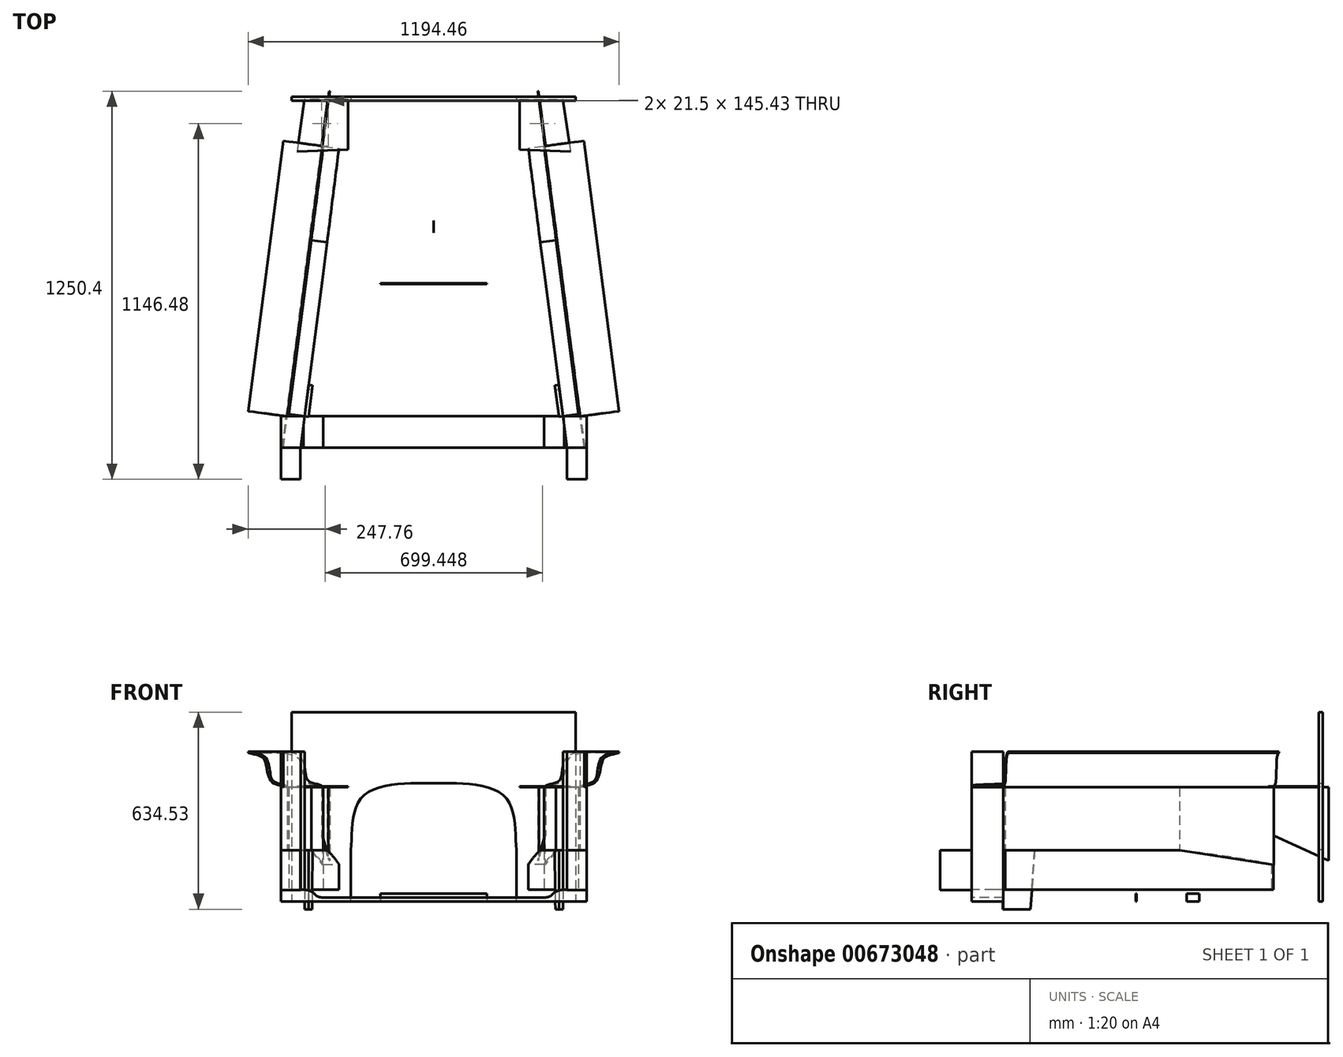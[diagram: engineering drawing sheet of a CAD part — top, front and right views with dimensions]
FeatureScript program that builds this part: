
annotation { "Feature Type Name" : "Feature", "Feature Type Description" : "" }
export const myFeature = defineFeature(function(context is Context, id is Id, definition is map)
    precondition{}
    {
        {
            var Q0;
            Q0=qCreatedBy(makeId("Top.planeOp"),FACE);
            var sketch = newSketch(context, id + "F0", { "sketchPlane" : qUnion([Q0])});
            skLineSegment(sketch, "E0.bottom", {"start": v(0, 0) * mm, "end": v(711.2, 0) * mm});
            skLineSegment(sketch, "E0.top", {"start": v(0, -101.6) * mm, "end": v(711.2, -101.6) * mm});
            skLineSegment(sketch, "E0.left", {"start": v(0, 0) * mm, "end": v(0, -101.6) * mm});
            skLineSegment(sketch, "E0.right", {"start": v(711.2, 0) * mm, "end": v(711.2, -101.6) * mm});
            skLineSegment(sketch, "E1", {"start": v(711.2, -101.6) * mm, "end": v(784.23, -101.6) * mm});
            skLineSegment(sketch, "E2", {"start": v(0, -101.6) * mm, "end": v(-73.03, -101.6) * mm});
            skLineSegment(sketch, "E3", {"start": v(711.2, 0) * mm, "end": v(771.52, 0) * mm});
            skLineSegment(sketch, "E4", {"start": v(0, 0) * mm, "end": v(-60.33, 0) * mm});
            skLineSegment(sketch, "E5", {"start": v(-60.33, 0) * mm, "end": v(-73.03, -101.6) * mm});
            skLineSegment(sketch, "E6", {"start": v(771.52, 0) * mm, "end": v(784.23, -101.6) * mm});
            skLineSegment(sketch, "E7", {"start": v(784.23, -101.6) * mm, "end": v(847.73, -101.6) * mm});
            skLineSegment(sketch, "E8", {"start": v(847.73, -101.6) * mm, "end": v(847.73, 0) * mm});
            skLineSegment(sketch, "E9", {"start": v(847.73, 0) * mm, "end": v(771.52, 0) * mm});
            skLineSegment(sketch, "E10", {"start": v(-73.03, -101.6) * mm, "end": v(-136.53, -101.6) * mm});
            skLineSegment(sketch, "E11", {"start": v(-136.53, -101.6) * mm, "end": v(-136.53, 0) * mm});
            skLineSegment(sketch, "E12", {"start": v(-136.53, 0) * mm, "end": v(-60.33, 0) * mm});
            skLineSegment(sketch, "E13", {"start": v(355.6, 0) * mm, "end": v(355.6, 428.63) * mm});
            skLineSegment(sketch, "E14", {"start": v(355.6, 428.63) * mm, "end": v(527.05, 428.63) * mm});
            skLineSegment(sketch, "E15", {"start": v(355.6, 428.63) * mm, "end": v(184.15, 428.63) * mm});
            skLineSegment(sketch, "E16", {"start": v(184.15, 428.63) * mm, "end": v(184.15, 426.09) * mm});
            skLineSegment(sketch, "E17", {"start": v(184.15, 426.09) * mm, "end": v(527.05, 426.09) * mm});
            skLineSegment(sketch, "E18", {"start": v(527.05, 426.09) * mm, "end": v(527.05, 428.63) * mm});
            skLineSegment(sketch, "E19", {"start": v(355.6, 428.63) * mm, "end": v(355.6, 438.15) * mm});
            skLineSegment(sketch, "E20", {"start": v(355.6, 438.15) * mm, "end": v(-3.17, 438.15) * mm});
            skLineSegment(sketch, "E21", {"start": v(355.6, 438.15) * mm, "end": v(714.35, 438.15) * mm});
            skLineSegment(sketch, "E22", {"start": v(-60.32, 0) * mm, "end": v(-3.17, 438.15) * mm});
            skLineSegment(sketch, "E23", {"start": v(714.35, 438.15) * mm, "end": v(771.52, 0) * mm});
            skLineSegment(sketch, "E24", {"start": v(-3.18, 438.15) * mm, "end": v(50.79, 862.83) * mm});
            skLineSegment(sketch, "E25", {"start": v(50.79, 862.83) * mm, "end": v(660.39, 862.83) * mm});
            skLineSegment(sketch, "E26", {"start": v(660.39, 862.83) * mm, "end": v(714.35, 438.15) * mm});
            skLineSegment(sketch, "E27", {"start": v(660.39, 862.83) * mm, "end": v(710.78, 869.23) * mm});
            skLineSegment(sketch, "E28", {"start": v(771.52, 0) * mm, "end": v(821.9, 6.57) * mm});
            skLineSegment(sketch, "E29", {"start": v(710.78, 869.23) * mm, "end": v(821.9, 6.57) * mm});
            skLineSegment(sketch, "E30", {"start": v(660.39, 862.83) * mm, "end": v(622.29, 862.83) * mm});
            skLineSegment(sketch, "E31", {"start": v(50.79, 862.83) * mm, "end": v(88.89, 862.83) * mm});
            skLineSegment(sketch, "E32", {"start": v(355.6, 0) * mm, "end": v(355.6, 1016) * mm});
            skLineSegment(sketch, "E33", {"start": v(355.6, 1016) * mm, "end": v(812.8, 1016) * mm});
            skLineSegment(sketch, "E34.MirrorCS", {"start": v(50.81, 862.83) * mm, "end": v(0.42, 869.23) * mm});
            skLineSegment(sketch, "E35.MirrorCS", {"start": v(0.42, 869.23) * mm, "end": v(-110.7, 6.57) * mm});
            skLineSegment(sketch, "E36.MirrorCS", {"start": v(-60.32, 0) * mm, "end": v(-110.7, 6.57) * mm});
            skLineSegment(sketch, "E37.MirrorCS", {"start": v(-136.53, 0) * mm, "end": v(-60.32, 0) * mm});
            skLineSegment(sketch, "E38.MirrorCS", {"start": v(-136.52, -101.6) * mm, "end": v(-136.52, 0) * mm});
            skLineSegment(sketch, "E39", {"start": v(355.6, 630.77) * mm, "end": v(355.85, 630.77) * mm});
            skLineSegment(sketch, "E40", {"start": v(355.85, 630.77) * mm, "end": v(355.85, 590.81) * mm});
            skLineSegment(sketch, "E41", {"start": v(355.85, 590.81) * mm, "end": v(355.6, 590.81) * mm});
            skLineSegment(sketch, "E42", {"start": v(355.6, 1016) * mm, "end": v(-101.6, 1016) * mm});
            skLineSegment(sketch, "E43", {"start": v(-101.6, 1016) * mm, "end": v(-101.6, 1028.7) * mm});
            skLineSegment(sketch, "E44", {"start": v(-101.6, 1028.7) * mm, "end": v(813.04, 1028.7) * mm});
            skLineSegment(sketch, "E45", {"start": v(813.04, 1028.7) * mm, "end": v(812.8, 1016) * mm});
            skSolve(sketch);
        }
        {
            var Q0;
            Q0=makeQuery(id+"F0.imprint","IMPRINT",FACE,{"disambiguationData":[TD([[makeQuery(id+"F0.imprint","IMPRINT",EDGE,{"derivedFrom":sQuery(id+"F0.wireOp",EDGE,"E0.top")}),1.0]])]});
            extrude(context, id + "F1", {"entities" : qUnion([Q0]), "depth" : 12.7 * mm, "offsetDistance" : 25.4 * mm});
        }
        {
            var Q0;
            Q0=makeQuery(id+"F0.imprint","IMPRINT",FACE,{"disambiguationData":[TD([[makeQuery(id+"F0.imprint","IMPRINT",EDGE,{"derivedFrom":sQuery(id+"F0.wireOp",EDGE,"E0.right")}),1.0]])]});
            extrude(context, id + "F2", {"entities" : qUnion([Q0]), "operationType" : NewBodyOperationType.ADD, "depth" : 38.1 * mm, "offsetDistance" : 25.4 * mm});
        }
        {
            var Q0;
            Q0=makeQuery(id+"F0.imprint","IMPRINT",FACE,{"disambiguationData":[TD([[makeQuery(id+"F0.imprint","IMPRINT",EDGE,{"derivedFrom":sQuery(id+"F0.wireOp",EDGE,"E6")}),1.0]])]});
            extrude(context, id + "F3", {"entities" : qUnion([Q0]), "operationType" : NewBodyOperationType.ADD, "depth" : 482.6 * mm, "offsetDistance" : 25.4 * mm});
        }
        {
            var Q0;
            Q0=makeQuery(id+"F0.imprint","IMPRINT",FACE,{"disambiguationData":[TD([[makeQuery(id+"F0.imprint","IMPRINT",EDGE,{"derivedFrom":sQuery(id+"F0.wireOp",EDGE,"E23")}),1.0]])]});
            extrude(context, id + "F4", {"entities" : qUnion([Q0]), "depth" : 165.1 * mm, "offsetDistance" : 25.4 * mm});
        }
        {
            var Q0;
            Q0=makeQuery(id+"F0.imprint","IMPRINT",FACE,{"disambiguationData":[TD([[makeQuery(id+"F0.imprint","IMPRINT",EDGE,{"derivedFrom":sQuery(id+"F0.wireOp",EDGE,"E23")}),1.0]])]});
            extrude(context, id + "F5", {"entities" : qUnion([Q0]), "operationType" : NewBodyOperationType.REMOVE, "depth" : 38.1 * mm, "offsetDistance" : 25.4 * mm});
        }
        {
            var Q0;
            Q0=makeQuery(id+"F4.opExtrude","SWEPT_FACE",FACE,{"disambiguationData":[OSD([sQuery(id+"F0.wireOp",EDGE,"E26")])]});
            var sketch = newSketch(context, id + "F6", { "sketchPlane" : qUnion([Q0])});
            skPoint(sketch, "E46.1.internal.snap0", {"position": v(-467.9, 143.2) * mm});
            skFitSpline(sketch, "E46", {"points": [v(-467.9, 165.1) * mm, v(-633.83, 143.2) * mm, v(-772.7, 119.15) * mm], "startDerivative": vector(-344.98, -40.08) * mm, "endDerivative": vector(-262.21, -52.17) * mm});
            skLineSegment(sketch, "E47", {"start": v(-772.7, 119.15) * mm, "end": v(-772.7, 165.1) * mm});
            skLineSegment(sketch, "E48", {"start": v(-772.7, 165.1) * mm, "end": v(-467.9, 165.1) * mm});
            skSolve(sketch);
        }
        {
            var Q0;
            Q0=makeQuery(id+"F6.imprint","IMPRINT",FACE,{"disambiguationData":[TD([[makeQuery(id+"F6.imprint","IMPRINT",EDGE,{"derivedFrom":sQuery(id+"F6.wireOp",EDGE,"E46")}),-1.0]])]});
            extrude(context, id + "F7", {"entities" : qUnion([Q0]), "operationType" : NewBodyOperationType.REMOVE, "oppositeDirection" : true, "depth" : 53.34 * mm, "offsetDistance" : 25.4 * mm});
        }
        {
            var Q0;
            Q0=makeQuery(id+"F4.opExtrude","CAP_FACE",FACE,{"disambiguationData":[OSD([sQuery(id+"F0.wireOp",EDGE,"E23"),sQuery(id+"F0.wireOp",EDGE,"E26"),sQuery(id+"F0.wireOp",EDGE,"E27"),sQuery(id+"F0.wireOp",EDGE,"E28"),sQuery(id+"F0.wireOp",EDGE,"E29")])],"isStart":false});
            var sketch = newSketch(context, id + "F8", { "sketchPlane" : qUnion([Q0])});
            skLineSegment(sketch, "E49", {"start": v(749.72, 566.93) * mm, "end": v(752.87, 567.33) * mm});
            skLineSegment(sketch, "E50", {"start": v(752.87, 567.33) * mm, "end": v(826.9, 0) * mm});
            skLineSegment(sketch, "E51", {"start": v(826.9, 0) * mm, "end": v(771.52, 0) * mm});
            skLineSegment(sketch, "E52", {"start": v(771.52, 0) * mm, "end": v(821.9, 6.57) * mm});
            skLineSegment(sketch, "E53", {"start": v(821.9, 6.57) * mm, "end": v(749.72, 566.93) * mm});
            skSolve(sketch);
        }
        {
            var Q0;
            Q0=makeQuery(id+"F8.imprint","IMPRINT",FACE,{"disambiguationData":[TD([[makeQuery(id+"F8.imprint","IMPRINT",EDGE,{"derivedFrom":sQuery(id+"F8.wireOp",EDGE,"E49")}),-1.0]])]});
            extrude(context, id + "F9", {"entities" : qUnion([Q0]), "operationType" : NewBodyOperationType.ADD, "depth" : 203.2 * mm, "offsetDistance" : 25.4 * mm});
        }
        {
            var Q0;
            Q0=makeQuery(id+"F3.boolean.opBoolean","MERGE",FACE,{"derivedFrom":[makeQuery(id+"F2.boolean.opBoolean","MERGE",FACE,{"derivedFrom":[makeQuery(id+"F1.opExtrude","SWEPT_FACE",FACE,{"disambiguationData":[OSD([sQuery(id+"F0.wireOp",EDGE,"E0.top")])]}),makeQuery(id+"F2.opExtrude","SWEPT_FACE",FACE,{"disambiguationData":[OSD([sQuery(id+"F0.wireOp",EDGE,"E1")])]})]}),makeQuery(id+"F3.opExtrude","SWEPT_FACE",FACE,{"disambiguationData":[OSD([sQuery(id+"F0.wireOp",EDGE,"E7")])]})]});
            var sketch = newSketch(context, id + "F10", { "sketchPlane" : qUnion([Q0])});
            skLineSegment(sketch, "E54", {"start": v(711.2, 12.7) * mm, "end": v(711.2, 38.1) * mm});
            skLineSegment(sketch, "E55", {"start": v(711.2, 38.1) * mm, "end": v(784.23, 38.1) * mm});
            skFitSpline(sketch, "E56", {"points": [v(784.23, 38.1) * mm, v(745.92, 30.04) * mm, v(734.41, 19.42) * mm, v(711.2, 12.7) * mm], "startDerivative": vector(-114.1, 5.7) * mm, "endDerivative": vector(-138.93, -12.85) * mm});
            skSolve(sketch);
        }
        {
            var Q0;
            {var subQ0=sQuery(id+"F10.wireOp",EDGE,"E54");Q0=makeQuery(id+"F10.imprint","IMPRINT",FACE,{"disambiguationData":[TD([[makeQuery(id+"F10.imprint","IMPRINT",EDGE,{"derivedFrom":subQ0}),1.0]])]});}
            extrude(context, id + "F11", {"entities" : qUnion([Q0]), "operationType" : NewBodyOperationType.REMOVE, "oppositeDirection" : true, "depth" : 101.6 * mm, "offsetDistance" : 25.4 * mm});
        }
        {
            var Q0;
            {var subQ0=sQuery(id+"F0.wireOp",EDGE,"E15");Q0=makeQuery(id+"F0.imprint","IMPRINT",FACE,{"disambiguationData":[TD([[makeQuery(id+"F0.imprint","IMPRINT",EDGE,{"derivedFrom":subQ0}),1.0]])]});}
            var Q1;
            {var subQ0=sQuery(id+"F0.wireOp",EDGE,"E14");Q1=makeQuery(id+"F0.imprint","IMPRINT",FACE,{"disambiguationData":[TD([[makeQuery(id+"F0.imprint","IMPRINT",EDGE,{"derivedFrom":subQ0}),-1.0]])]});}
            extrude(context, id + "F12", {"entities" : qUnion([Q0, Q1]), "depth" : 25.4 * mm, "offsetDistance" : 25.4 * mm});
        }
        {
            var Q0;
            {var subQ0=sQuery(id+"F0.wireOp",EDGE,"E39");Q0=makeQuery(id+"F0.imprint","IMPRINT",FACE,{"disambiguationData":[TD([[makeQuery(id+"F0.imprint","IMPRINT",EDGE,{"derivedFrom":subQ0}),-1.0]])]});}
            extrude(context, id + "F13", {"entities" : qUnion([Q0]), "depth" : 25.4 * mm, "offsetDistance" : 25.4 * mm});
        }
        {
            var Q0;
            Q0=makeQuery(id+"F4.opExtrude","SWEPT_BODY",BODY,{"disambiguationData":[OSD([sQuery(id+"F0.wireOp",EDGE,"E23"),sQuery(id+"F0.wireOp",EDGE,"E26"),sQuery(id+"F0.wireOp",EDGE,"E27"),sQuery(id+"F0.wireOp",EDGE,"E28"),sQuery(id+"F0.wireOp",EDGE,"E29")])]});
            var Q1;
            Q1=makeQuery(id+"F1.opExtrude","SWEPT_BODY",BODY,{"disambiguationData":[OSD([sQuery(id+"F0.wireOp",EDGE,"E0.bottom"),sQuery(id+"F0.wireOp",EDGE,"E0.top"),sQuery(id+"F0.wireOp",EDGE,"E0.left"),sQuery(id+"F0.wireOp",EDGE,"E0.right")])]});
            var Q2;
            Q2=makeQuery(id+"F13.opExtrude","SWEPT_FACE",FACE,{"disambiguationData":[OSD([sQuery(id+"F0.wireOp",EDGE,"E32")])]});
            mirror(context, id + "F14", {"operationType" : NewBodyOperationType.ADD, "entities" : qUnion([Q0, Q1]), "mirrorPlane" : qUnion([Q2])});
        }
        {
            var Q0;
            Q0=makeQuery(id+"F9.opExtrude","SWEPT_FACE",FACE,{"disambiguationData":[OSD([sQuery(id+"F8.wireOp",EDGE,"E50")])]});
            var sketch = newSketch(context, id + "F15", { "sketchPlane" : qUnion([Q0])});
            skLineSegment(sketch, "E57", {"start": v(465.15, 368.3) * mm, "end": v(770.95, 368.3) * mm});
            skLineSegment(sketch, "E58", {"start": v(770.95, 368.3) * mm, "end": v(770.95, 118.46) * mm});
            skLineSegment(sketch, "E59", {"start": v(-107, 482.07) * mm, "end": v(770.95, 482.07) * mm});
            skLineSegment(sketch, "E60", {"start": v(770.95, 482.07) * mm, "end": v(770.95, 368.3) * mm});
            skLineSegment(sketch, "E61", {"start": v(465.15, 368.3) * mm, "end": v(465.15, 165.1) * mm});
            skLineSegment(sketch, "E62", {"start": v(465.15, 165.1) * mm, "end": v(770.95, 118.46) * mm});
            skLineSegment(sketch, "E63", {"start": v(-107, 482.07) * mm, "end": v(-107, 368.3) * mm});
            skLineSegment(sketch, "E64", {"start": v(-107, 368.3) * mm, "end": v(465.15, 368.3) * mm});
            skLineSegment(sketch, "E65", {"start": v(770.95, 368.3) * mm, "end": v(948.75, 368.3) * mm});
            skLineSegment(sketch, "E66", {"start": v(948.75, 368.3) * mm, "end": v(948.75, 131.53) * mm});
            skLineSegment(sketch, "E67", {"start": v(948.75, 131.53) * mm, "end": v(770.95, 211.96) * mm});
            skSolve(sketch);
        }
        {
            var Q0;
            Q0=makeQuery(id+"F15.imprint","IMPRINT",FACE,{"disambiguationData":[TD([[makeQuery(id+"F15.imprint","IMPRINT",EDGE,{"derivedFrom":sQuery(id+"F15.wireOp",EDGE,"E57")}),-1.0]])]});
            extrude(context, id + "F16", {"entities" : qUnion([Q0]), "oppositeDirection" : true, "depth" : 2.54 * mm, "offsetDistance" : 25.4 * mm});
        }
        {
            var Q0;
            Q0=makeQuery(id+"F15.imprint","IMPRINT",FACE,{"disambiguationData":[TD([[makeQuery(id+"F15.imprint","IMPRINT",EDGE,{"derivedFrom":sQuery(id+"F15.wireOp",EDGE,"E57")}),1.0]])]});
            extrude(context, id + "F17", {"entities" : qUnion([Q0]), "depth" : 127 * mm, "offsetDistance" : 25.4 * mm});
        }
        {
            var Q0;
            Q0=makeQuery(id+"F17.opExtrude","SWEPT_FACE",FACE,{"disambiguationData":[OSD([sQuery(id+"F15.wireOp",EDGE,"E60")])]});
            var sketch = newSketch(context, id + "F18", { "sketchPlane" : qUnion([Q0])});
            skFitSpline(sketch, "E68", {"points": [v(-819.95, 368.3) * mm, v(-869.16, 392.24) * mm, v(-946.95, 482.07) * mm], "startDerivative": vector(-53.79, 96.96) * mm, "endDerivative": vector(-444.07, 0) * mm});
            skLineSegment(sketch, "E69", {"start": v(-946.95, 482.07) * mm, "end": v(-946.95, 478.9) * mm});
            skLineSegment(sketch, "E70", {"start": v(-819.95, 368.3) * mm, "end": v(-823.13, 368.3) * mm});
            skFitSpline(sketch, "E71", {"points": [v(-946.95, 478.9) * mm, v(-892.3, 451.57) * mm, v(-864.36, 380.9) * mm, v(-823.13, 368.3) * mm], "startDerivative": vector(317.97, -76.6) * mm, "endDerivative": vector(-33.51, -59.88) * mm});
            skLineSegment(sketch, "E72", {"start": v(-946.95, 482.07) * mm, "end": v(-819.95, 482.07) * mm});
            skLineSegment(sketch, "E73", {"start": v(-819.95, 482.07) * mm, "end": v(-819.95, 368.3) * mm});
            skLineSegment(sketch, "E74", {"start": v(-823.13, 368.3) * mm, "end": v(-946.95, 368.3) * mm});
            skLineSegment(sketch, "E75", {"start": v(-946.95, 368.3) * mm, "end": v(-946.95, 478.9) * mm});
            skSolve(sketch);
        }
        {
            var Q0;
            Q0=makeQuery(id+"F18.imprint","IMPRINT",FACE,{"disambiguationData":[TD([[makeQuery(id+"F18.imprint","IMPRINT",EDGE,{"derivedFrom":sQuery(id+"F18.wireOp",EDGE,"E68")}),-1.0]])]});
            var Q1;
            Q1=makeQuery(id+"F18.imprint","IMPRINT",FACE,{"disambiguationData":[TD([[makeQuery(id+"F18.imprint","IMPRINT",EDGE,{"derivedFrom":sQuery(id+"F18.wireOp",EDGE,"E71")}),-1.0]])]});
            extrude(context, id + "F19", {"entities" : qUnion([Q0, Q1]), "operationType" : NewBodyOperationType.REMOVE, "oppositeDirection" : true, "depth" : 1016 * mm, "offsetDistance" : 25.4 * mm});
        }
        {
            var Q0;
            Q0=makeQuery(id+"F16.opExtrude","SWEPT_BODY",BODY,{"disambiguationData":[OSD([sQuery(id+"F15.wireOp",EDGE,"E57"),sQuery(id+"F15.wireOp",EDGE,"E58"),sQuery(id+"F15.wireOp",EDGE,"E61"),sQuery(id+"F15.wireOp",EDGE,"E62")])]});
            var Q1;
            Q1=makeQuery(id+"F17.opExtrude","SWEPT_BODY",BODY,{"disambiguationData":[OSD([sQuery(id+"F15.wireOp",EDGE,"E57"),sQuery(id+"F15.wireOp",EDGE,"E59"),sQuery(id+"F15.wireOp",EDGE,"E60"),sQuery(id+"F15.wireOp",EDGE,"E63"),sQuery(id+"F15.wireOp",EDGE,"E64")])]});
            var Q2;
            Q2=makeQuery(id+"F13.opExtrude","SWEPT_FACE",FACE,{"disambiguationData":[OSD([sQuery(id+"F0.wireOp",EDGE,"E32")])]});
            mirror(context, id + "F20", {"operationType" : NewBodyOperationType.ADD, "entities" : qUnion([Q0, Q1]), "mirrorPlane" : qUnion([Q2])});
        }
        {
            var Q0;
            Q0=makeQuery(id+"F0.imprint","IMPRINT",FACE,{"disambiguationData":[TD([[makeQuery(id+"F0.imprint","IMPRINT",EDGE,{"derivedFrom":sQuery(id+"F0.wireOp",EDGE,"E33")}),1.0]])]});
            extrude(context, id + "F21", {"entities" : qUnion([Q0]), "depth" : 609.6 * mm, "offsetDistance" : 25.4 * mm});
        }
        {
            var Q0;
            {var subQ0=sQuery(id+"F15.wireOp",EDGE,"E65");Q0=makeQuery(id+"F15.imprint","IMPRINT",FACE,{"disambiguationData":[TD([[makeQuery(id+"F15.imprint","IMPRINT",EDGE,{"derivedFrom":subQ0}),-1.0]])]});}
            extrude(context, id + "F22", {"entities" : qUnion([Q0]), "operationType" : NewBodyOperationType.ADD, "depth" : 2.54 * mm, "offsetDistance" : 25.4 * mm});
        }
        {
            var Q0;
            Q0=makeQuery(id+"F21.opExtrude","SWEPT_FACE",FACE,{"disambiguationData":[OSD([sQuery(id+"F0.wireOp",EDGE,"E33"),sQuery(id+"F0.wireOp",EDGE,"E42")])]});
            var sketch = newSketch(context, id + "F23", { "sketchPlane" : qUnion([Q0])});
            skLineSegment(sketch, "E76", {"start": v(355.6, 0) * mm, "end": v(622.3, 0) * mm});
            skLineSegment(sketch, "E77", {"start": v(355.6, 0) * mm, "end": v(88.9, 0) * mm});
            skLineSegment(sketch, "E78", {"start": v(622.3, 0) * mm, "end": v(622.3, 165.82) * mm});
            skLineSegment(sketch, "E79", {"start": v(622.3, 165.82) * mm, "end": v(696.88, 165.82) * mm});
            skLineSegment(sketch, "E80", {"start": v(355.6, 609.6) * mm, "end": v(355.6, 381) * mm});
            skFitSpline(sketch, "E81", {"points": [v(355.6, 381) * mm, v(581.3, 340.9) * mm, v(622.3, 165.82) * mm], "startDerivative": vector(346.5, 0.28) * mm, "endDerivative": vector(34.55, -341.6) * mm});
            skFitSpline(sketch, "E82.MirrorCS", {"points": [v(355.6, 381) * mm, v(129.9, 340.9) * mm, v(88.9, 165.82) * mm], "startDerivative": vector(-346.5, 0.28) * mm, "endDerivative": vector(-34.55, -341.6) * mm});
            skLineSegment(sketch, "E83.MirrorCS", {"start": v(88.9, 0) * mm, "end": v(88.9, 165.82) * mm});
            skLineSegment(sketch, "E84.MirrorCS", {"start": v(88.9, 165.82) * mm, "end": v(14.32, 165.82) * mm});
            skSolve(sketch);
        }
        {
            var Q0;
            Q0=makeQuery(id+"F23.imprint","IMPRINT",FACE,{"disambiguationData":[TD([[makeQuery(id+"F23.imprint","IMPRINT",EDGE,{"derivedFrom":sQuery(id+"F23.wireOp",EDGE,"E76")}),-1.0]])]});
            extrude(context, id + "F24", {"entities" : qUnion([Q0]), "operationType" : NewBodyOperationType.REMOVE, "oppositeDirection" : true, "depth" : 25.4 * mm, "offsetDistance" : 25.4 * mm});
        }
        {
            var Q0;
            Q0=makeQuery(id+"F21.opExtrude","SWEPT_BODY",BODY,{"disambiguationData":[OSD([sQuery(id+"F0.wireOp",EDGE,"E33"),sQuery(id+"F0.wireOp",EDGE,"E42"),sQuery(id+"F0.wireOp",EDGE,"E43"),sQuery(id+"F0.wireOp",EDGE,"pW7Q4AVf-aAkG-GrlD-G3aG-ndCrtpSd0GbX"),sQuery(id+"F0.wireOp",EDGE,"s7aEdVuP-2PAB-8kZs-Fb0w-fgtPghY44Bxq")])]});
            var Q1;
            Q1=makeQuery(id+"F13.opExtrude","SWEPT_FACE",FACE,{"disambiguationData":[OSD([sQuery(id+"F0.wireOp",EDGE,"E32")])]});
            mirror(context, id + "F25", {"operationType" : NewBodyOperationType.ADD, "entities" : qUnion([Q0]), "mirrorPlane" : qUnion([Q1])});
        }
        {
            var Q0;
            {var subQ0=sQuery(id+"F0.wireOp",EDGE,"E0.top");var subQ1=makeQuery(id+"F1.opExtrude","CAP_EDGE",EDGE,{"disambiguationData":[OSD([subQ0])],"isStart":false});Q0=makeQuery(id+"F10.imprint","IMPRINT",FACE,{"disambiguationData":[TD([[makeQuery(id+"F10.imprint","IMPRINT",EDGE,{"derivedFrom":subQ1}),-1.0]])]});}
            var sketch = newSketch(context, id + "F26", { "sketchPlane" : qUnion([Q0])});
            skLineSegment(sketch, "E85.bottom", {"start": v(784.8, 165.71) * mm, "end": v(847.86, 165.71) * mm});
            skLineSegment(sketch, "E85.top", {"start": v(784.8, 36.57) * mm, "end": v(847.86, 36.57) * mm});
            skLineSegment(sketch, "E85.left", {"start": v(784.8, 165.71) * mm, "end": v(784.8, 36.57) * mm});
            skLineSegment(sketch, "E85.right", {"start": v(847.86, 165.71) * mm, "end": v(847.86, 36.57) * mm});
            skSolve(sketch);
        }
        {
            var Q0;
            {var subQ0=sQuery(id+"F26.wireOp",EDGE,"E85.left");Q0=makeQuery(id+"F26.imprint","IMPRINT",FACE,{"disambiguationData":[TD([[makeQuery(id+"F26.imprint","IMPRINT",EDGE,{"derivedFrom":subQ0}),1.0]])]});}
            extrude(context, id + "F27", {"entities" : qUnion([Q0]), "operationType" : NewBodyOperationType.ADD, "depth" : 101.6 * mm, "offsetDistance" : 25.4 * mm});
        }
        {
            var Q0;
            Q0=makeQuery(id+"F1.opExtrude","SWEPT_BODY",BODY,{"disambiguationData":[OSD([sQuery(id+"F0.wireOp",EDGE,"E0.bottom"),sQuery(id+"F0.wireOp",EDGE,"E0.top"),sQuery(id+"F0.wireOp",EDGE,"E0.left"),sQuery(id+"F0.wireOp",EDGE,"E0.right")])]});
            var Q1;
            Q1=makeQuery(id+"F13.opExtrude","SWEPT_FACE",FACE,{"disambiguationData":[OSD([sQuery(id+"F0.wireOp",EDGE,"E32")])]});
            mirror(context, id + "F28", {"entities" : qUnion([Q0]), "mirrorPlane" : qUnion([Q1])});
        }
        {
            var Q0;
            {var subQ0=sQuery(id+"F15.wireOp",EDGE,"E58");var subQ3=sQuery(id+"F15.wireOp",EDGE,"E65");Q0=makeQuery(id+"F25.opPattern","COPY",FACE,{"derivedFrom":makeQuery(id+"F22.boolean.opBoolean","SPLIT",FACE,{"disambiguationData":[TD([makeQuery(id+"F22.opExtrude","SWEPT_FACE",FACE,{"disambiguationData":[OSD([subQ0])]})])],"derivedFrom":makeQuery(id+"F22.opExtrude","SWEPT_FACE",FACE,{"disambiguationData":[OSD([subQ3])]})}),"instanceName":"1"});}
            var sketch = newSketch(context, id + "F29", { "sketchPlane" : qUnion([Q0])});
            skLineSegment(sketch, "E86", {"start": v(79.76, 859.55) * mm, "end": v(79.76, 1019.9) * mm});
            skLineSegment(sketch, "E87", {"start": v(79.76, 1019.9) * mm, "end": v(-60.12, 1019.9) * mm});
            skLineSegment(sketch, "E88", {"start": v(-60.12, 1019.9) * mm, "end": v(-84.03, 852.97) * mm});
            skLineSegment(sketch, "E89", {"start": v(-84.03, 852.97) * mm, "end": v(79.76, 859.55) * mm});
            skSolve(sketch);
        }
        {
            var Q0;
            Q0=makeQuery(id+"F29.imprint","IMPRINT",FACE,{"disambiguationData":[TD([[makeQuery(id+"F29.imprint","IMPRINT",EDGE,{"derivedFrom":sQuery(id+"F29.wireOp",EDGE,"E86")}),1.0]])]});
            extrude(context, id + "F30", {"entities" : qUnion([Q0]), "depth" : 2.54 * mm, "offsetDistance" : 25.4 * mm});
        }
        {
            var Q0;
            Q0=makeQuery(id+"F30.opExtrude","SWEPT_BODY",BODY,{"disambiguationData":[OSD([sQuery(id+"F0.wireOp",EDGE,"E33"),sQuery(id+"F0.wireOp",EDGE,"E42"),sQuery(id+"F15.wireOp",EDGE,"E57"),sQuery(id+"F15.wireOp",EDGE,"E58"),sQuery(id+"F15.wireOp",EDGE,"E60"),sQuery(id+"F15.wireOp",EDGE,"E65"),sQuery(id+"F29.wireOp",EDGE,"E86"),sQuery(id+"F29.wireOp",EDGE,"E87"),sQuery(id+"F29.wireOp",EDGE,"E88"),sQuery(id+"F29.wireOp",EDGE,"E89")])]});
            var Q1;
            Q1=makeQuery(id+"F13.opExtrude","SWEPT_FACE",FACE,{"disambiguationData":[OSD([sQuery(id+"F0.wireOp",EDGE,"E40")])]});
            mirror(context, id + "F31", {"entities" : qUnion([Q0]), "mirrorPlane" : qUnion([Q1])});
        }
        {
            var Q0;
            Q0=makeQuery(id+"F14.opPattern","COPY",FACE,{"derivedFrom":makeQuery(id+"F4.opExtrude","SWEPT_FACE",FACE,{"disambiguationData":[OSD([sQuery(id+"F0.wireOp",EDGE,"E23")])]}),"instanceName":"1"});
            var sketch = newSketch(context, id + "F32", { "sketchPlane" : qUnion([Q0])});
            skLineSegment(sketch, "E90", {"start": v(-7.8, 165.1) * mm, "end": v(93.8, 165.1) * mm});
            skLineSegment(sketch, "E91", {"start": v(93.8, 165.1) * mm, "end": v(80.45, -24.93) * mm});
            skLineSegment(sketch, "E92", {"start": v(80.45, -24.93) * mm, "end": v(-7.8, -24.93) * mm});
            skLineSegment(sketch, "E93", {"start": v(-7.8, -24.93) * mm, "end": v(-7.8, 165.1) * mm});
            skSolve(sketch);
        }
        {
            var Q0;
            {var subQ0=sQuery(id+"F32.wireOp",EDGE,"E90");Q0=makeQuery(id+"F32.imprint","IMPRINT",FACE,{"disambiguationData":[TD([[makeQuery(id+"F32.imprint","IMPRINT",EDGE,{"derivedFrom":subQ0}),1.0]])]});}
            var Q1;
            {var subQ0=sQuery(id+"F32.wireOp",EDGE,"E92");Q1=makeQuery(id+"F32.imprint","IMPRINT",FACE,{"disambiguationData":[TD([[makeQuery(id+"F32.imprint","IMPRINT",EDGE,{"derivedFrom":subQ0}),-1.0]])]});}
            extrude(context, id + "F33", {"entities" : qUnion([Q0, Q1]), "depth" : 12.7 * mm, "offsetDistance" : 25.4 * mm});
        }
        {
            var Q0;
            Q0=makeQuery(id+"F33.opExtrude","SWEPT_BODY",BODY,{"disambiguationData":[OSD([sQuery(id+"F32.wireOp",EDGE,"E90"),sQuery(id+"F32.wireOp",EDGE,"E91"),sQuery(id+"F32.wireOp",EDGE,"E92"),sQuery(id+"F32.wireOp",EDGE,"E93")])]});
            var Q1;
            Q1=makeQuery(id+"F13.opExtrude","SWEPT_FACE",FACE,{"disambiguationData":[OSD([sQuery(id+"F0.wireOp",EDGE,"E32")])]});
            mirror(context, id + "F34", {"entities" : qUnion([Q0]), "mirrorPlane" : qUnion([Q1])});
        }
    });
